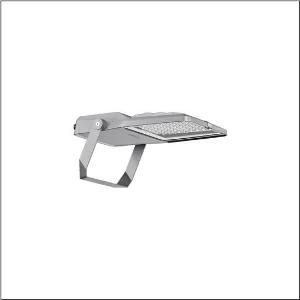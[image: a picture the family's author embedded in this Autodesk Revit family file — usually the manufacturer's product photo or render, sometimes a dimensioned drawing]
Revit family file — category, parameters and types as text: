
# Revit family: floodlight_fl_21_mini___pl64_5xa7775b2e1a_35e6
name_source: partatom
category: Lighting Fixtures
units: mm (PartAtom-declared; Revit-internal decimal feet)

## family parameters
Cut with Voids When Loaded = No
Host = Face
Light Source = No
Part Type = Normal
Room Calculation Point = No
Round Connector Dimension = Use Diameter
Shared = No

## types (1)
- --- (1 x LED, 6010 lm, 45.7 W, 3000K)
    Apparent Load = 46 VA
    CIE Flux Codes = 28 80 98 100 100
    Color Rendering = 70
    Color Temperature = 3000K
    Default Elevation = 1800 mm
    Description = Floodlight FL 21 mini, floodlight, primary light control with lens, of PMMA, primary optical cover: protective disc, of toughened safety glass, transparent, light distribution: PL64, light emission: direct distribution, installation type: surface-mounted, LED, High Power LED, rated luminous flux: 6.010lm, luminous efficacy: 132lm/W, light colour: 730, colour temperature: 3000K, control: flexible luminous flux parameterisation, time-dependent luminous flux control, constant luminous flux control, overheat protection, presetting dimming logarithmic, with terminal, 6-pole, mains connection: 220..240V, AC, 50/60Hz, start of lifetime: 46W, end of service life: 48W, reduction: 22W, luminaire housing, of diecast aluminium, powder-coated, Siteco® metallic grey (DB 702S), corrosivity category C5 mid according to DIN EN ISO 12944, sealing non-destructively replaceable, mounting bracket, of steel, galvanised, powder-coated, Siteco® metallic grey (DB 702S), Smart Interface above, protection rating (complete): IP66, insulation class (complete): insulation class II (safety insulation), certification: CE, ENEC, VDE, protection symbol: D, impact resistance: IK08, permissible operating ambient temperature: -40..+40°C, permissible operating ambient temperature for outdoor applications: -40..+50°C, standard: DIN EN 12944, LABS conformity tested according to VDMA 24364:2018-05, packaging unit: 1 piece

Light Distribution: PL64
    Height = 70 mm
    Lamp = 1 x LED
    Lamp Light Flux = 6010 lm
    Lamp Power = 45.7 W
    Lamp count = 1
    Length = 485 mm
    Luminous efficacy = 132 lm/W
    Manufacturer = Siteco
    ModVariant = No
    Model = 5XA7775B2E1A
    Number of Poles = 1
    OnlyDefault = Yes
    Power Factor = 1
    Product Name = Floodlight FL 21 mini | PL64
    Product group = floodlight | pylon annexe
    ProductGroupID = 6200
    Protection Class = Protection class II
    Protection Degree = IP 66
    RLX_Detail_Level = 1
    RLX_Emergency_Light_Flux = 0 lm
    RLX_Emergency_Type = 0
    RLX_Emergency_Type_DB = No
    RlxData = <blob elided: 95909 chars, md5=22b5a374>
    Socket = socket
    Standby Power = 0 W
    System Light Flux = 6010 lm
    System Power = 46 W
    Type Comments = factory setting: luminous flux: 100 % | dim-lin: 254 | 463 mA
    Type Image = l_1006845.jpg
    URL = http://relux.com
    VarID = @adj_115729
    Voltage = 0 V
    Weight = 0.00 kg
    Width = 337 mm

## geometry (parser evidence)
native form markers: Blend x4, Sweep x14
no freeform markers — native parametric forms only
